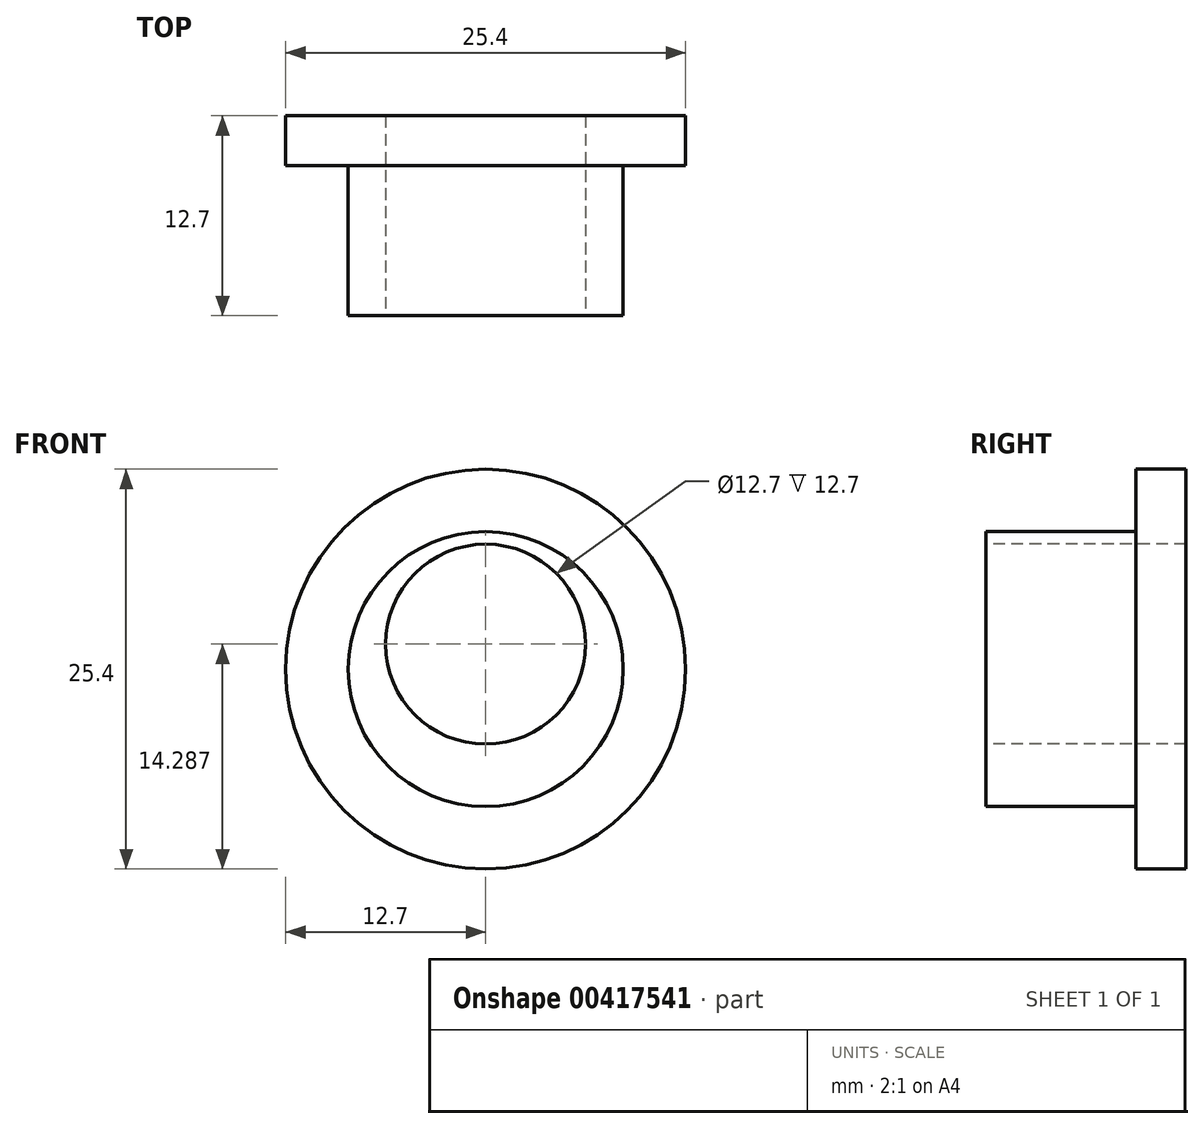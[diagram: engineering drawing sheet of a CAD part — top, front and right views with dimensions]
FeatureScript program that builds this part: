
annotation { "Feature Type Name" : "Feature", "Feature Type Description" : "" }
export const myFeature = defineFeature(function(context is Context, id is Id, definition is map)
    precondition{}
    {
        {
            var Q0;
            Q0=qCreatedBy(makeId("Front.planeOp"),FACE);
            var sketch = newSketch(context, id + "F0", { "sketchPlane" : qUnion([Q0])});
            skCircle(sketch, "E0", {"center": v(0, 0) * mm, "radius": 12.7 * mm});
            skCircle(sketch, "E1", {"center": v(0, 0) * mm, "radius": 8.73 * mm});
            skPoint(sketch, "E2", {"position": v(0, 1.59) * mm});
            skSolve(sketch);
        }
        {
            var Q0;
            Q0=makeQuery(id+"F0.imprint","IMPRINT",FACE,{"disambiguationData":[TD([[makeQuery(id+"F0.imprint","IMPRINT",EDGE,{"derivedFrom":sQuery(id+"F0.wireOp",EDGE,"E1")}),1.0]])]});
            var Q1;
            Q1=makeQuery(id+"F0.imprint","IMPRINT",FACE,{"disambiguationData":[TD([[makeQuery(id+"F0.imprint","IMPRINT",EDGE,{"derivedFrom":sQuery(id+"F0.wireOp",EDGE,"E0")}),1.0]])]});
            extrude(context, id + "F1", {"entities" : qUnion([Q0, Q1]), "depth" : 3.17 * mm});
        }
        {
            var Q0;
            Q0=makeQuery(id+"F1.opExtrude","CAP_FACE",FACE,{"disambiguationData":[OSD([sQuery(id+"F0.wireOp",EDGE,"E0")])],"isStart":false});
            var sketch = newSketch(context, id + "F2", { "sketchPlane" : qUnion([Q0])});
            skCircle(sketch, "E3", {"center": v(0, 0) * mm, "radius": 8.73 * mm});
            skSolve(sketch);
        }
        {
            var Q0;
            Q0=makeQuery(id+"F2.imprint","IMPRINT",FACE,{"disambiguationData":[TD([[makeQuery(id+"F2.imprint","IMPRINT",EDGE,{"derivedFrom":sQuery(id+"F2.wireOp",EDGE,"E3")}),1.0]])]});
            extrude(context, id + "F3", {"entities" : qUnion([Q0]), "operationType" : NewBodyOperationType.ADD, "depth" : 9.52 * mm});
        }
        {
            var Q0;
            Q0=makeQuery(id+"F3.opExtrude","CAP_FACE",FACE,{"disambiguationData":[OSD([sQuery(id+"F2.wireOp",EDGE,"E3")])],"isStart":false});
            var sketch = newSketch(context, id + "F4", { "sketchPlane" : qUnion([Q0])});
            skPoint(sketch, "E4", {"position": v(0, 1.59) * mm});
            skSolve(sketch);
        }
        {
            var Q0;
            Q0=sQuery(id+"F4.wireOp",VERTEX,"E4");
            var Q1;
            Q1=makeQuery(id+"F1.opExtrude","SWEPT_BODY",BODY,{"disambiguationData":[OSD([sQuery(id+"F0.wireOp",EDGE,"E0")])]});
            hole(context, id + "F5", {"style" : HoleStyle.SIMPLE, "endStyle" : HoleEndStyle.THROUGH, "holeDiameter" : 12.7 * mm, "isTappedThrough" : true, "tappedDepth" : 12.7 * mm, "tapClearance" : 3, "locations" : qUnion([Q0]), "scope" : qUnion([Q1])});
        }
    });
